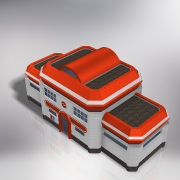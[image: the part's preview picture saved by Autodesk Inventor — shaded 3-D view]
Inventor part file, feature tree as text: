
AUTODESK INVENTOR PART (.ipt)
format: ipt  version: 2017.3 (Build 213256000, 256)  size: 1,937,920 bytes
history: native  units: in
note: dims shown in document units (in); Inventor stores cm internally (conversion verified against a paired STEP export)
features: sketch x29, extrude x28, projected_geometry x13, split x9, chamfer x6, mirror x5, sweep x2, emboss x1, fillet x1, other x1
ambient origin geometry x8: Origin, YZ Plane, XZ Plane, XY Plane, X Axis, Y Axis, Z Axis, Center Point
bodies: Solid1 (feature_tree)
feature tree (95):
  extrude  "Extrusion1"  Depth=36.0in TaperAngle=45.0deg
  chamfer  "Chamfer1"  Distance=120.0in
  extrude  "Extrusion2"  Depth=84.0in
  chamfer  "Chamfer2"  Distance=30.0in Angle=45.0deg
  emboss  "Emboss1"
  sketch  "Sketch3"  dims[d8=36.0in d9=84.0in]
  extrude  "Extrusion5"  Depth=16.0in TaperAngle=0.0deg
  extrude  "Extrusion6"  Depth=1.0in TaperAngle=0.0deg
  extrude  "Extrusion7"  Depth=6.0in
  sketch  "Sketch5"  dims[d12=10.0in]
  sweep  "Sweep1"
  mirror  "Mirror1"
  sweep  "Sweep2"
  extrude  "Extrusion8"  Depth=12.0in
  extrude  "Extrusion9"  Depth=1.75in
  extrude  "Extrusion10"  Depth=54.577in TaperAngle=0.0deg
  extrude  "Extrusion11"  Depth=11.0in
  chamfer  "Chamfer4"  Distance=14.0in
  extrude  "Extrusion12"  Depth=0.8in
  extrude  "Extrusion13"  Depth=2.5in TaperAngle=0.0deg
  chamfer  "Chamfer5"  Distance=8.0in Angle=45.0deg
  mirror  "Mirror2"
  mirror  "Mirror3"
  sketch  "Sketch12"  dims[d34=12.0in d35=6.0in]
  split  "Split1"
  split  "Split2"
  split  "Split3"
  split  "Split4"
  sketch  "Sketch13"  dims[d36=0.0in d37=0.0in d38=6.0in]
  split  "Split5"
  split  "Split6"
  split  "Split7"
  sketch  "Sketch14"  dims[d39=6.0in d40=9.8996in]
  extrude  "Extrusion14"  Depth=10.985in
  extrude  "Extrusion15"  Depth=1.6in
  extrude  "Extrusion16"  Depth=2.5in TaperAngle=0.0deg
  fillet  "Fillet1"  Radius=3.0in
  extrude  "Extrusion17"  Depth=2.0in
  extrude  "Extrusion18"  Depth=188.0in
  chamfer  "Chamfer6"  Distance=3.0in
  sketch  "Sketch18"  dims[d49=70.087in d50=0.0in d51=11.0in]
  extrude  "Extrusion19"  Depth=188.0in
  extrude  "Extrusion20"  Depth=188.0in
  extrude  "Extrusion21"  Depth=188.0in
  mirror  "Mirror4"
  mirror  "Mirror5"
  sketch  "Sketch20"  dims[d58=0.8in d59=0.8in]
  extrude  "Extrusion22"  Depth=188.0in
  extrude  "Extrusion23"  Depth=188.0in
  extrude  "Extrusion24"  Depth=188.0in
  extrude  "Extrusion25"  Depth=188.0in
  chamfer  "Chamfer7"  Distance=5.5in
  sketch  "Sketch23"  dims[d77=10.9847in d78=1.6in]
  split  "Split8"
  split  "Split9"
  extrude  "Extrusion26"  Depth=188.0in
  extrude  "Extrusion27"  Depth=188.0in
  extrude  "Extrusion28"  Depth=188.0in
  other  "Floor Plane"
  sketch  "Sketch28"  dims[d94=0.7in d95=0.7in d96=3.0in d97=3.0in d98=3.0in d99=1.75in d100=1.75in d101=1.75in d102=1.75in d103=1.75in d104=5.5in d105=5.5in d106=80.0in d107=45.0in d108=2.0in d109=4.0in d110=1.5in d111=1.5in d112=56.0in d113=25.0in d114=1.5in d115=1.0in d116=0.0in d117=5.0in d118=0.0in d119=2.0in d120=2.0in d121=2.0in d122=2.0in d123=1.0in d124=1.0in d125=1.0in d126=1.0in d127=1.0in d128=1.0in d129=1.0in d130=1.0in d131=1.0in d132=1.0in d133=1.0in d134=1.0in d135=1.0in d136=1.0in d137=1.0in d138=1.0in d139=1.0in d140=0.0in d141=6.0in d142=214.791in d143=0.0in d144=15.0in d145=15.0in d146=8.0in d147=8.0in d148=0.0in d149=3.0in d150=0.125in d151=45.0deg d152=28.0in d153=120.0in d154=1.5in d155=1.0in d156=0.0in d157=5.0in d158=0.0in d159=2.0in d160=1.0in d161=0.0in d162=120.0in d163=28.0in d164=1.5in d165=1.0in d166=0.0in d167=5.0in d168=0.0in d169=2.0in d170=1.0in d171=0.0in d172=10.0in d174=16.0in d176=16.0in d177=60.9868in d178=4.0in d179=4.0in d180=8.712in d181=8.712in d182=4.0in d183=8.712in d184=8.712in d185=8.712in d186=153.612in d187=0.0in d188=8.0in d189=0.125in d190=45.0deg d191=14.0in d192=14.0in d193=0.1in d194=0.0in d195=1.0in d196=0.0in d197=0.25in d198=0.0in d201=0.5in d202=115.3125in d203=0.0in d204=0.5in d205=0.5in d206=0.5in d207=0.5in d208=0.5in d209=0.5in d210=0.5in d211=0.5in d212=0.5in d213=0.5in d214=188.0in d215=0.0in]
  extrude  "Extrusion29"  Depth=188.0in
  extrude  "Extrusion30"  Depth=188.0in
  sketch  "Sketch1"  dims[d0=192.0in d1=0.0in d2=36.0in d3=0.125in d4=45.0deg]
  sketch  "Sketch2"  dims[d5=650.0in d6=120.0in d7=0.0in]
  sketch  "Sketch4"  dims[d10=18.0in]
  sketch  "3D Sketch1"
  sketch  "3D Sketch2"
  sketch  "Sketch6"  dims[d13=26.0in]
  projected_geometry  "Projected Loop1"
  projected_geometry  "Projected Loop2"
  sketch  "Sketch7"  dims[d14=3.75in]
  sketch  "Sketch8"  dims[d15=2.5in]
  projected_geometry  "Projected Loop3"
  sketch  "Sketch9"  dims[d16=2.5in d21=30.0in d22=0.125in d23=45.0deg]
  sketch  "Sketch10"  dims[d24=6.0in d25=0.0in d26=16.0in d27=0.0in]
  projected_geometry  "Projected Loop4"
  sketch  "Sketch11"  dims[d28=6.0in d29=0.0in d30=1.0in d31=6.0in d32=0.0in d33=0.0in]
  sketch  "Sketch15"  dims[d41=9.8996in d42=12.0in]
  projected_geometry  "Projected Loop5"
  projected_geometry  "Projected Loop6"
  projected_geometry  "Projected Loop7"
  projected_geometry  "Projected Loop8"
  projected_geometry  "Projected Loop9"
  sketch  "Sketch16"  dims[d43=1.75in d44=1.75in]
  sketch  "Sketch17"  dims[d45=0.0in d46=0.0in d47=54.577in d48=0.0in]
  projected_geometry  "Projected Loop10"
  sketch  "Sketch19"  dims[d52=11.0in d53=14.0in d54=0.0in]
  projected_geometry  "Projected Loop11"
  sketch  "Sketch21"  dims[d60=1.5748in d62=23.5696in d63=1.5748in d65=23.5696in d68=2.5in d69=0.0in d70=8.0in d71=0.125in d72=45.0deg]
  projected_geometry  "Projected Loop12"
  sketch  "Sketch22"  dims[d73=14.0in d74=0.0in d75=10.985in]
  sketch  "Sketch24"  dims[d79=1.5748in d81=23.5696in d82=0.3937in d84=1.0in d86=2.5in d87=0.0in]
  sketch  "Sketch25"  dims[d88=8.0in d89=0.125in d90=45.0deg d91=3.0in]
  sketch  "Sketch26"  dims[d92=3.0in d93=2.0in]
  projected_geometry  "Projected Loop13"
